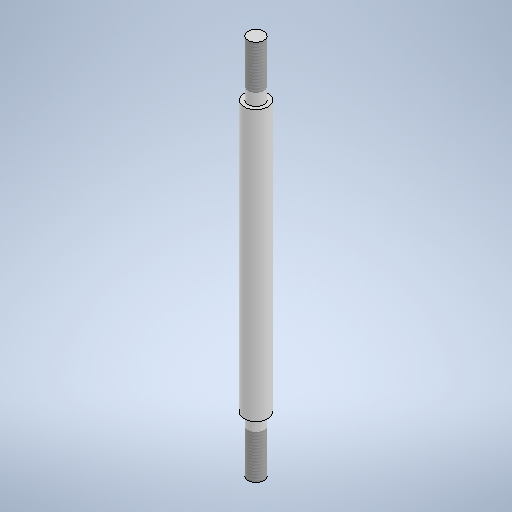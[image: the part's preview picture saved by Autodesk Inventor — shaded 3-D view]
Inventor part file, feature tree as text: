
AUTODESK INVENTOR PART (.ipt)
format: ipt  version: 2025 (Build 290162010, 162A)  size: 273,408 bytes
history: native  units: mm
features: thread x2, revolve x1, sketch x1
ambient origin geometry x8: Origin, YZ Plane, XZ Plane, XY Plane, X Axis, Y Axis, Z Axis, Center Point
bodies: Volumenkörper1 (feature_tree)
feature tree (4):
  revolve  "Umdrehung1"
  thread  "Gewinde1"  [1 undecoded]
  thread  "Gewinde2"  [1 undecoded]
  sketch  "Skizze1"  dims[d2=14.0mm d3=4.0mm d4=6.0mm d5=90.0deg d6=11.0mm d7=0.0mm d8=11.0mm d9=0.0mm]
note: 2 required parameter values undecoded (feature->parameter linkage not recoverable at this tier; creation-order binding heuristic only, values carry confidence <= 0.55)
